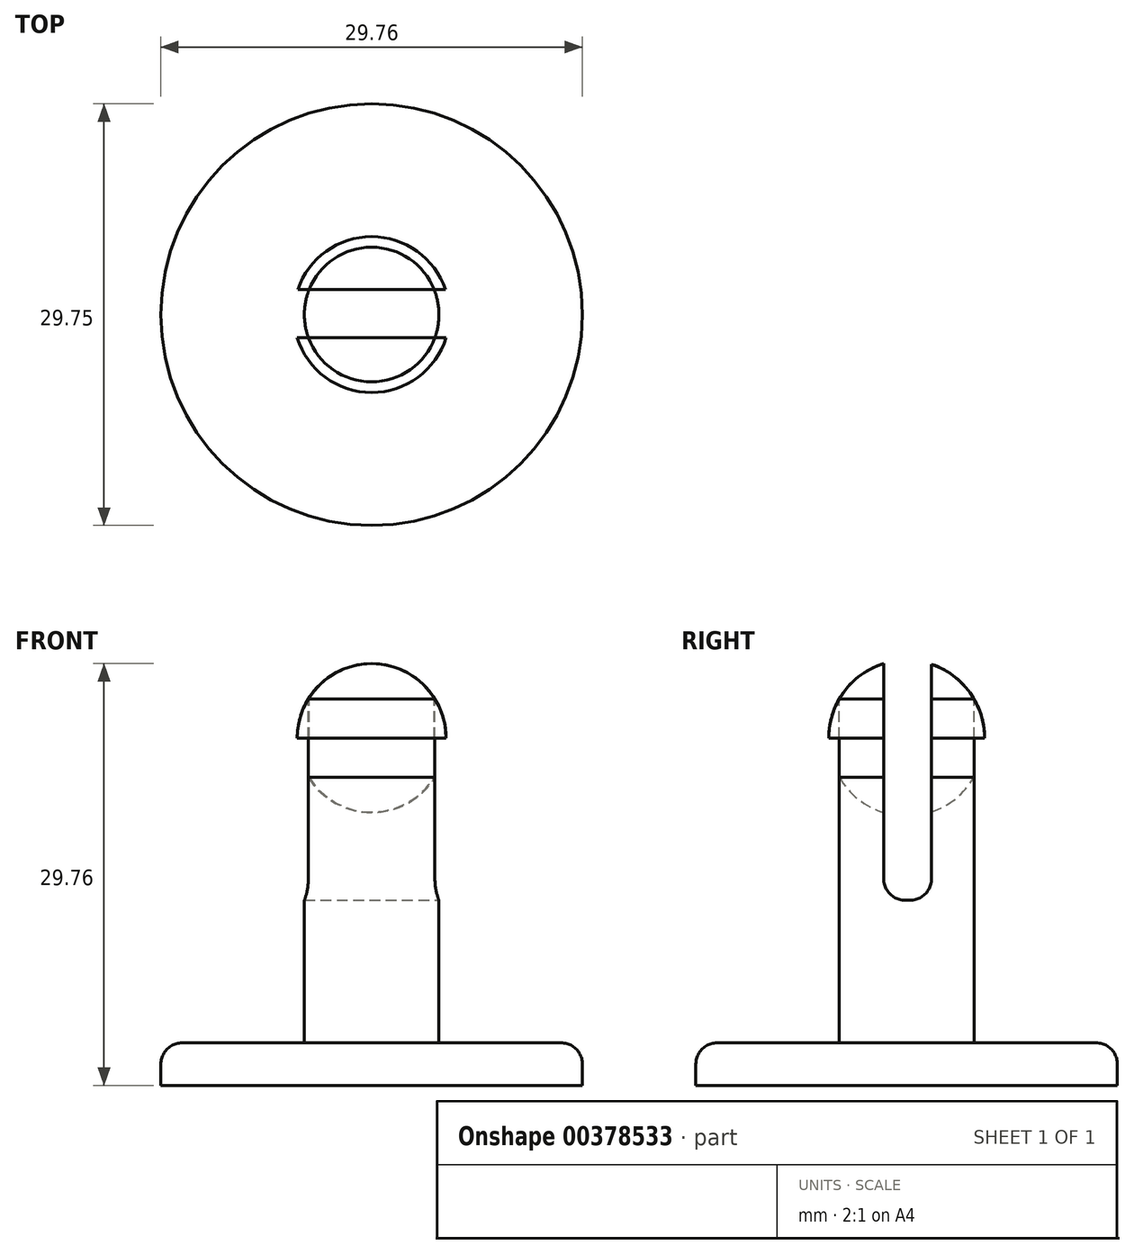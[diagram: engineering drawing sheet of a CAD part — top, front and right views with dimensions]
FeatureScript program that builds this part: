
annotation { "Feature Type Name" : "Feature", "Feature Type Description" : "" }
export const myFeature = defineFeature(function(context is Context, id is Id, definition is map)
    precondition{}
    {
        {
            var Q0;
            Q0=qCreatedBy(makeId("Right.planeOp"),FACE);
            var sketch = newSketch(context, id + "F0", { "sketchPlane" : qUnion([Q0])});
            skLineSegment(sketch, "E0.bottom", {"start": v(-4.43, 0) * mm, "end": v(5.07, 0) * mm});
            skLineSegment(sketch, "E0.top", {"start": v(-4.43, 27) * mm, "end": v(5.07, 27) * mm});
            skLineSegment(sketch, "E0.left", {"start": v(-4.43, 0) * mm, "end": v(-4.43, 27) * mm});
            skLineSegment(sketch, "E0.right", {"start": v(5.07, 0) * mm, "end": v(5.07, 27) * mm});
            skCircle(sketch, "E1", {"center": v(0.32, 21.5) * mm, "radius": 5.5 * mm});
            skPoint(sketch, "E1.centerSnap0", {"position": v(0.32, 27) * mm});
            skLineSegment(sketch, "E2.bottom", {"start": v(-1.08, 27) * mm, "end": v(1.72, 27) * mm});
            skLineSegment(sketch, "E2.top", {"start": v(-1.08, 11.41) * mm, "end": v(1.72, 11.41) * mm});
            skLineSegment(sketch, "E2.left", {"start": v(-1.08, 27) * mm, "end": v(-1.08, 11.41) * mm});
            skLineSegment(sketch, "E2.right", {"start": v(1.72, 27) * mm, "end": v(1.72, 11.41) * mm});
            skLineSegment(sketch, "E3", {"start": v(-6.96, 21.5) * mm, "end": v(10.65, 21.5) * mm});
            skLineSegment(sketch, "E4.bottom", {"start": v(15.2, 0) * mm, "end": v(-14.56, 0) * mm});
            skLineSegment(sketch, "E4.top", {"start": v(15.2, -3) * mm, "end": v(-14.56, -3) * mm});
            skLineSegment(sketch, "E4.left", {"start": v(15.2, 0) * mm, "end": v(15.2, -3) * mm});
            skLineSegment(sketch, "E4.right", {"start": v(-14.56, 0) * mm, "end": v(-14.56, -3) * mm});
            skPoint(sketch, "E4.middle", {"position": v(0.32, -1.5) * mm});
            skPoint(sketch, "E4.middle.positionSnap0", {"position": v(0.32, 0) * mm});
            skPoint(sketch, "E4.cornerSnap0", {"position": v(0.32, 0) * mm});
            skPoint(sketch, "E4.centerSnap0", {"position": v(0.32, 0) * mm});
            skLineSegment(sketch, "E5", {"start": v(0.32, 25.11) * mm, "end": v(0.32, -11.67) * mm});
            skSolve(sketch);
        }
        {
            var Q0;
            {var subQ7=sQuery(id+"F0.wireOp",EDGE,"E4.bottom");var subQ8=sQuery(id+"F0.wireOp",EDGE,"E0.left");var subQ9=makeQuery(id+"F0.imprint","INTERSECT",VERTEX,{"derivedFrom":[subQ8,subQ7]});Q0=makeQuery(id+"F0.imprint","IMPRINT",FACE,{"disambiguationData":[TD([[makeQuery(id+"F0.imprint","IMPRINT",EDGE,{"disambiguationData":[TD([[subQ9,-1.0]])],"derivedFrom":subQ8}),-1.0]])]});}
            var Q1;
            {var subQ0=sQuery(id+"F0.wireOp",EDGE,"E1");var subQ1=sQuery(id+"F0.wireOp",EDGE,"E0.right");var subQ2=makeQuery(id+"F0.imprint","INTERSECT",VERTEX,{"disambiguationData":[OD(0.0)],"derivedFrom":[subQ1,subQ0]});Q1=makeQuery(id+"F0.imprint","IMPRINT",FACE,{"disambiguationData":[TD([[makeQuery(id+"F0.imprint","IMPRINT",EDGE,{"disambiguationData":[TD([[subQ2,-1.0]])],"derivedFrom":subQ1}),1.0]])]});}
            var Q2;
            {var subQ0=sQuery(id+"F0.wireOp",EDGE,"E1");var subQ1=sQuery(id+"F0.wireOp",EDGE,"E0.right");var subQ2=makeQuery(id+"F0.imprint","INTERSECT",VERTEX,{"disambiguationData":[OD(1.0)],"derivedFrom":[subQ1,subQ0]});Q2=makeQuery(id+"F0.imprint","IMPRINT",FACE,{"disambiguationData":[TD([[makeQuery(id+"F0.imprint","IMPRINT",EDGE,{"disambiguationData":[TD([[subQ2,1.0]])],"derivedFrom":subQ1}),1.0]])]});}
            var Q3;
            {var subQ0=sQuery(id+"F0.wireOp",EDGE,"E1");var subQ1=sQuery(id+"F0.wireOp",EDGE,"E0.right");var subQ2=makeQuery(id+"F0.imprint","INTERSECT",VERTEX,{"disambiguationData":[OD(1.0)],"derivedFrom":[subQ1,subQ0]});Q3=makeQuery(id+"F0.imprint","IMPRINT",FACE,{"disambiguationData":[TD([[makeQuery(id+"F0.imprint","IMPRINT",EDGE,{"disambiguationData":[TD([[subQ2,1.0]])],"derivedFrom":subQ1}),-1.0]])]});}
            var Q4;
            {var subQ0=sQuery(id+"F0.wireOp",EDGE,"E1");var subQ1=sQuery(id+"F0.wireOp",EDGE,"E0.left");var subQ2=makeQuery(id+"F0.imprint","INTERSECT",VERTEX,{"disambiguationData":[OD(1.0)],"derivedFrom":[subQ1,subQ0]});Q4=makeQuery(id+"F0.imprint","IMPRINT",FACE,{"disambiguationData":[TD([[makeQuery(id+"F0.imprint","IMPRINT",EDGE,{"disambiguationData":[TD([[subQ2,1.0]])],"derivedFrom":subQ1}),-1.0]])]});}
            var Q5;
            {var subQ0=sQuery(id+"F0.wireOp",EDGE,"E1");var subQ1=sQuery(id+"F0.wireOp",EDGE,"E0.left");var subQ2=makeQuery(id+"F0.imprint","INTERSECT",VERTEX,{"disambiguationData":[OD(0.0)],"derivedFrom":[subQ1,subQ0]});Q5=makeQuery(id+"F0.imprint","IMPRINT",FACE,{"disambiguationData":[TD([[makeQuery(id+"F0.imprint","IMPRINT",EDGE,{"disambiguationData":[TD([[subQ2,-1.0]])],"derivedFrom":subQ1}),-1.0]])]});}
            var Q6;
            {var subQ0=sQuery(id+"F0.wireOp",EDGE,"E1");var subQ1=sQuery(id+"F0.wireOp",EDGE,"E0.left");var subQ2=makeQuery(id+"F0.imprint","INTERSECT",VERTEX,{"disambiguationData":[OD(1.0)],"derivedFrom":[subQ1,subQ0]});Q6=makeQuery(id+"F0.imprint","IMPRINT",FACE,{"disambiguationData":[TD([[makeQuery(id+"F0.imprint","IMPRINT",EDGE,{"disambiguationData":[TD([[subQ2,1.0]])],"derivedFrom":subQ1}),1.0]])]});}
            var Q7;
            {var subQ0=sQuery(id+"F0.wireOp",EDGE,"E4.left");Q7=makeQuery(id+"F0.imprint","IMPRINT",FACE,{"disambiguationData":[TD([[makeQuery(id+"F0.imprint","IMPRINT",EDGE,{"derivedFrom":subQ0}),-1.0]])]});}
            var Q8;
            Q8=sQuery(id+"F0.wireOp",EDGE,"E5");
            revolve(context, id + "F1", {"entities" : qUnion([Q0, Q1, Q2, Q3, Q4, Q5, Q6, Q7]), "axis" : qUnion([Q8]), "revolveType" : RevolveType.FULL});
        }
        {
            var Q0;
            Q0=qCreatedBy(makeId("Right.planeOp"),FACE);
            var sketch = newSketch(context, id + "F2", { "sketchPlane" : qUnion([Q0])});
            skLineSegment(sketch, "E6.bottom", {"start": v(-1.3, 32.98) * mm, "end": v(2.07, 32.98) * mm});
            skLineSegment(sketch, "E6.top", {"start": v(-1.3, 10.07) * mm, "end": v(2.07, 10.07) * mm});
            skLineSegment(sketch, "E6.left", {"start": v(-1.3, 32.98) * mm, "end": v(-1.3, 10.07) * mm});
            skLineSegment(sketch, "E6.right", {"start": v(2.07, 32.98) * mm, "end": v(2.07, 10.07) * mm});
            skPoint(sketch, "E6.middle", {"position": v(0.38, 21.52) * mm});
            skSolve(sketch);
        }
        {
            var Q0;
            Q0=makeQuery(id+"F2.imprint","IMPRINT",FACE,{"disambiguationData":[TD([[makeQuery(id+"F2.imprint","IMPRINT",EDGE,{"derivedFrom":sQuery(id+"F2.wireOp",EDGE,"E6.bottom")}),-1.0]])]});
            extrude(context, id + "F3", {"entities" : qUnion([Q0]), "operationType" : NewBodyOperationType.REMOVE, "oppositeDirection" : true, "depth" : 25 * mm, "hasSecondDirection" : true, "secondDirectionOppositeDirection" : false, "secondDirectionDepth" : 25 * mm});
        }
        {
            var Q0;
            Q0=makeQuery(id+"F3.boolean.opBoolean","COPY",EDGE,{"derivedFrom":makeQuery(id+"F3.opExtrude","SWEPT_EDGE",EDGE,{"disambiguationData":[OSD([sQuery(id+"F2.wireOp",EDGE,"E6.top"),sQuery(id+"F2.wireOp",EDGE,"E6.right")])]})});
            var Q1;
            Q1=makeQuery(id+"F3.boolean.opBoolean","COPY",EDGE,{"derivedFrom":makeQuery(id+"F3.opExtrude","SWEPT_EDGE",EDGE,{"disambiguationData":[OSD([sQuery(id+"F2.wireOp",EDGE,"E6.top"),sQuery(id+"F2.wireOp",EDGE,"E6.left")])]})});
            var Q2;
            Q2=makeQuery(id+"F1.opRevolve","SWEPT_EDGE",EDGE,{"disambiguationData":[OSD([sQuery(id+"F0.wireOp",EDGE,"E4.bottom"),sQuery(id+"F0.wireOp",EDGE,"E4.left")])]});
            fillet(context, id + "F4", {"entities" : qUnion([Q0, Q1, Q2]), "radius" : 1.5 * mm, "tangentPropagation" : true, "allowEdgeOverflow" : false});
        }
    });
